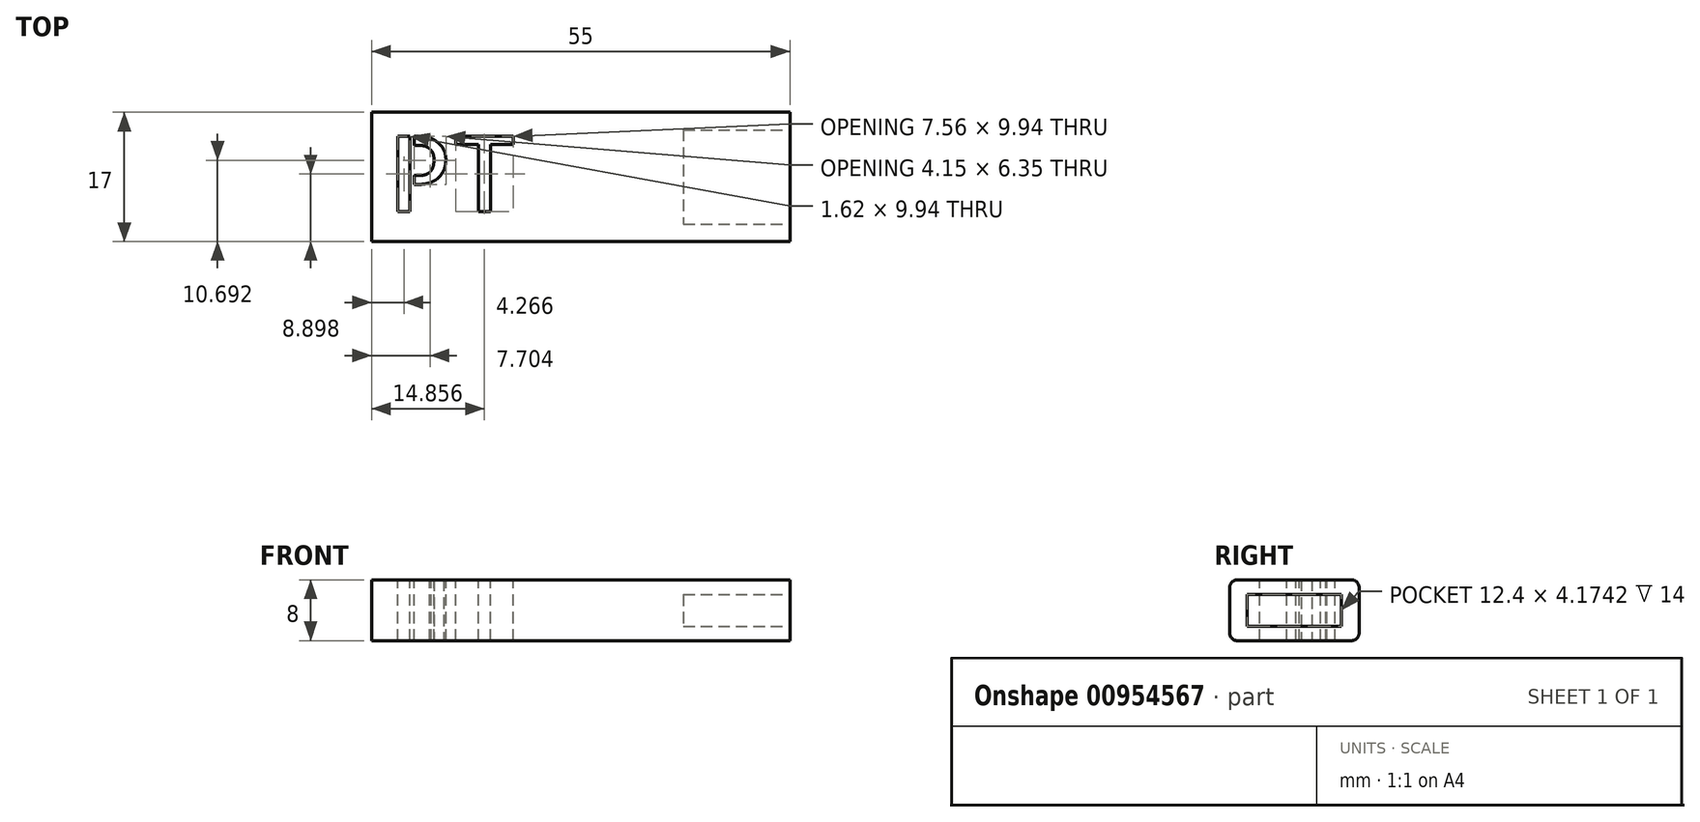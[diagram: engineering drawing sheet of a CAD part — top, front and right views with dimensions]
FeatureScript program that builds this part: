
annotation { "Feature Type Name" : "Feature", "Feature Type Description" : "" }
export const myFeature = defineFeature(function(context is Context, id is Id, definition is map)
    precondition{}
    {
        {
            var Q0;
            Q0=qCreatedBy(makeId("Front.planeOp"),FACE);
            var sketch = newSketch(context, id + "F0", { "sketchPlane" : qUnion([Q0])});
            skLineSegment(sketch, "E0.bottom", {"start": v(-7.5, 4) * mm, "end": v(7.5, 4) * mm});
            skLineSegment(sketch, "E0.top", {"start": v(-7.5, -4) * mm, "end": v(7.5, -4) * mm});
            skLineSegment(sketch, "E0.left", {"start": v(-8.5, 3) * mm, "end": v(-8.5, -3) * mm});
            skLineSegment(sketch, "E0.right", {"start": v(8.5, 3) * mm, "end": v(8.5, -3) * mm});
            skPoint(sketch, "E0.middle", {"position": v(0, 0) * mm});
            skPoint(sketch, "E1.visualSharp", {"position": v(-8.5, 4) * mm});
            skArc(sketch, "E1.filletArc", {"start": v(-7.5, 4) * mm, "mid": v(-8.2, 3.7) * mm, "end": v(-8.5, 3) * mm});
            skPoint(sketch, "E2.visualSharp", {"position": v(8.5, 4) * mm});
            skArc(sketch, "E2.filletArc", {"start": v(8.5, 3) * mm, "mid": v(8.2, 3.7) * mm, "end": v(7.5, 4) * mm});
            skPoint(sketch, "E3.visualSharp", {"position": v(8.5, -4) * mm});
            skArc(sketch, "E3.filletArc", {"start": v(7.5, -4) * mm, "mid": v(8.2, -3.7) * mm, "end": v(8.5, -3) * mm});
            skPoint(sketch, "E4.visualSharp", {"position": v(-8.5, -4) * mm});
            skArc(sketch, "E4.filletArc", {"start": v(-8.5, -3) * mm, "mid": v(-8.2, -3.7) * mm, "end": v(-7.5, -4) * mm});
            skSolve(sketch);
        }
        {
            var Q0;
            Q0 = qSketchRegion(id + "F0", true);
            extrude(context, id + "F1", {"entities" : qUnion([Q0]), "depth" : 55 * mm, "offsetDistance" : 25 * mm});
        }
        {
            var Q0;
            Q0=qCreatedBy(makeId("Front.planeOp"),FACE);
            var sketch = newSketch(context, id + "F2", { "sketchPlane" : qUnion([Q0])});
            skLineSegment(sketch, "E5.bottom", {"start": v(-6.2, 2.09) * mm, "end": v(6.2, 2.09) * mm});
            skLineSegment(sketch, "E5.top", {"start": v(-6.2, -2.09) * mm, "end": v(6.2, -2.09) * mm});
            skLineSegment(sketch, "E5.left", {"start": v(-6.2, 2.09) * mm, "end": v(-6.2, -2.09) * mm});
            skLineSegment(sketch, "E5.right", {"start": v(6.2, 2.09) * mm, "end": v(6.2, -2.09) * mm});
            skPoint(sketch, "E5.middle", {"position": v(0, 0) * mm});
            skSolve(sketch);
        }
        {
            var Q0;
            Q0 = qSketchRegion(id + "F2", true);
            extrude(context, id + "F3", {"entities" : qUnion([Q0]), "operationType" : NewBodyOperationType.REMOVE, "depth" : 14 * mm, "offsetDistance" : 25 * mm});
        }
        {
            var Q0;
            Q0=makeQuery(id+"F1.opExtrude","SWEPT_BODY",BODY,{"disambiguationData":[OSD([sQuery(id+"F0.wireOp",EDGE,"E0.bottom"),sQuery(id+"F0.wireOp",EDGE,"E0.top"),sQuery(id+"F0.wireOp",EDGE,"E0.left"),sQuery(id+"F0.wireOp",EDGE,"E0.right"),sQuery(id+"F0.wireOp",EDGE,"E1.filletArc"),sQuery(id+"F0.wireOp",EDGE,"E2.filletArc"),sQuery(id+"F0.wireOp",EDGE,"E3.filletArc"),sQuery(id+"F0.wireOp",EDGE,"E4.filletArc")])]});
            var Q1;
            Q1=makeQuery(id+"F1.opExtrude","CAP_EDGE",EDGE,{"disambiguationData":[OSD([sQuery(id+"F0.wireOp",EDGE,"E0.right")])],"isStart":false});
            transform(context, id + "F4", {"entities" : qUnion([Q0]), "transformType" : TransformType.ROTATION, "transformAxis" : qUnion([Q1]), "angle" : 90 * degree, "makeCopy" : false});
        }
        {
            var Q0;
            Q0=makeQuery(id+"F1.opExtrude","SWEPT_FACE",FACE,{"disambiguationData":[OSD([sQuery(id+"F0.wireOp",EDGE,"E0.bottom")])]});
            var sketch = newSketch(context, id + "F5", { "sketchPlane" : qUnion([Q0])});
            skText(sketch, "E6", { "text": "PT", "fontName": "AllertaStencil-Regular.ttf"});
            const initialGuessF5  = {"E6": [0.01073, -0.05107, 1, 0, 0.00994]};
            skSetInitialGuess(sketch, initialGuessF5);
            skSolve(sketch);
        }
        {
            var Q0;
            Q0 = qSketchRegion(id + "F5", true);
            extrude(context, id + "F6", {"entities" : qUnion([Q0]), "operationType" : NewBodyOperationType.REMOVE, "oppositeDirection" : true, "depth" : 25 * mm, "offsetDistance" : 25 * mm});
        }
    });
